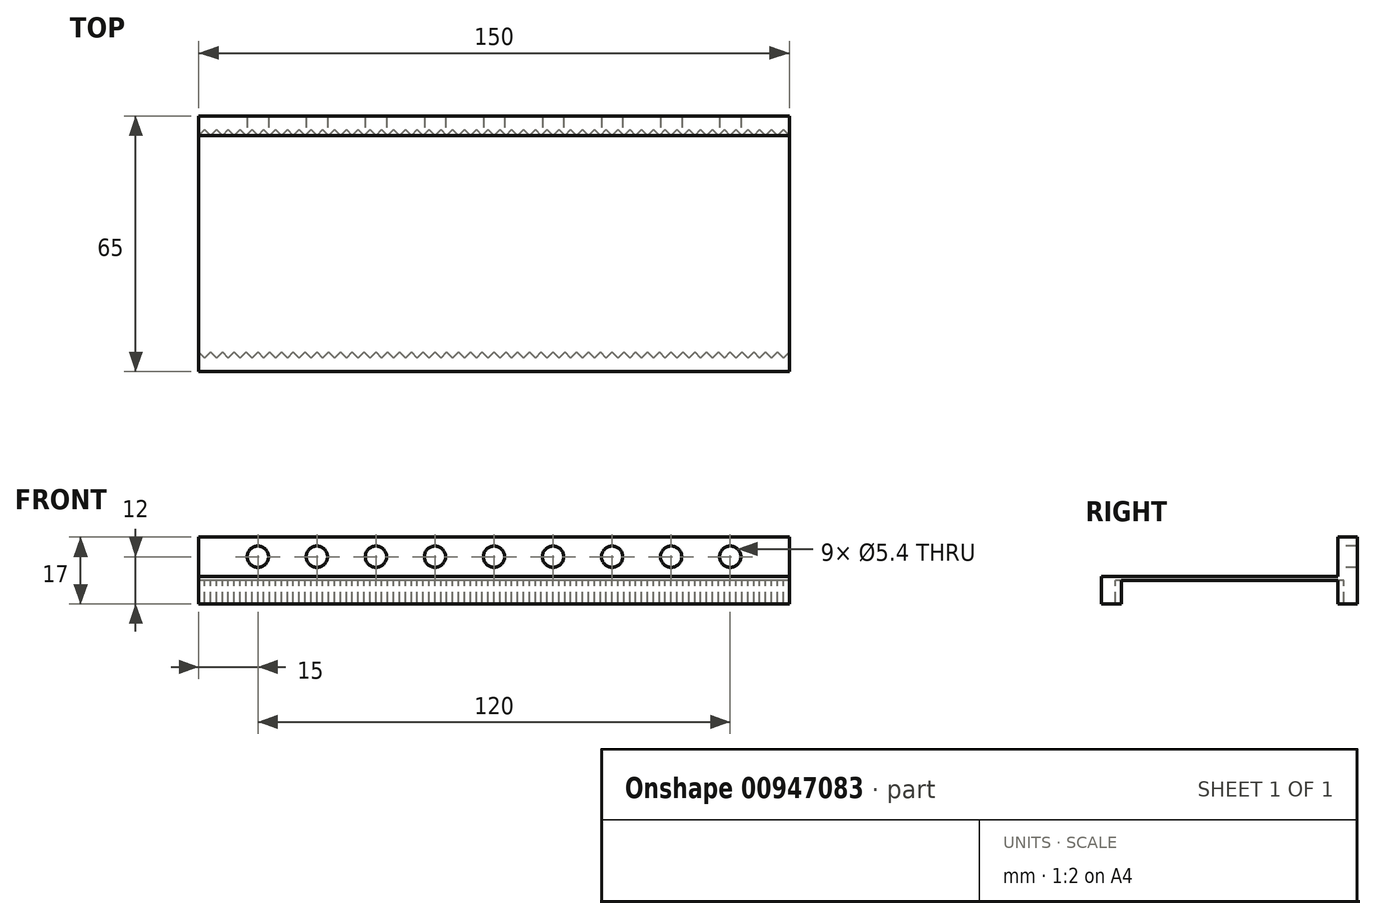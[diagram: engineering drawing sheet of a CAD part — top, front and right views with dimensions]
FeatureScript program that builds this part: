
annotation { "Feature Type Name" : "Feature", "Feature Type Description" : "" }
export const myFeature = defineFeature(function(context is Context, id is Id, definition is map)
    precondition{}
    {
        {
            var Q0;
            Q0=qCreatedBy(makeId("Top.planeOp"),FACE);
            var sketch = newSketch(context, id + "F0", { "sketchPlane" : qUnion([Q0])});
            skLineSegment(sketch, "E0.bottom", {"start": v(75, 32.5) * mm, "end": v(-75, 32.5) * mm});
            skLineSegment(sketch, "E0.top", {"start": v(75, -32.5) * mm, "end": v(-75, -32.5) * mm});
            skLineSegment(sketch, "E0.left", {"start": v(75, 32.5) * mm, "end": v(75, -32.5) * mm});
            skLineSegment(sketch, "E0.right", {"start": v(-75, 32.5) * mm, "end": v(-75, -32.5) * mm});
            skPoint(sketch, "E0.middle", {"position": v(0, 0) * mm});
            skSolve(sketch);
        }
        {
            var Q0;
            Q0 = qSketchRegion(id + "F0", true);
            extrude(context, id + "F1", {"entities" : qUnion([Q0]), "depth" : 1 * mm, "offsetDistance" : 25 * mm});
        }
        {
            var Q0;
            Q0=makeQuery(id+"F1.opExtrude","CAP_FACE",FACE,{"disambiguationData":[OSD([sQuery(id+"F0.wireOp",EDGE,"E0.bottom"),sQuery(id+"F0.wireOp",EDGE,"E0.top"),sQuery(id+"F0.wireOp",EDGE,"E0.left"),sQuery(id+"F0.wireOp",EDGE,"E0.right")])],"isStart":true});
            var sketch = newSketch(context, id + "F2", { "sketchPlane" : qUnion([Q0])});
            skLineSegment(sketch, "E1.bottom", {"start": v(75, -32.5) * mm, "end": v(-75, -32.5) * mm});
            skLineSegment(sketch, "E1.top", {"start": v(75, -27.5) * mm, "end": v(-75, -27.5) * mm, "construction": true});
            skLineSegment(sketch, "E1.left", {"start": v(75, -32.5) * mm, "end": v(75, -27.5) * mm});
            skLineSegment(sketch, "E1.right", {"start": v(-75, -32.5) * mm, "end": v(-75, -27.5) * mm});
            skLineSegment(sketch, "E2.bottom", {"start": v(75, 32.5) * mm, "end": v(-75, 32.5) * mm});
            skLineSegment(sketch, "E2.top", {"start": v(75, 27.5) * mm, "end": v(-75, 27.5) * mm, "construction": true});
            skLineSegment(sketch, "E2.left", {"start": v(75, 32.5) * mm, "end": v(75, 27.5) * mm});
            skLineSegment(sketch, "E2.right", {"start": v(-75, 32.5) * mm, "end": v(-75, 27.5) * mm});
            skLineSegment(sketch, "E3", {"start": v(75, -27.5) * mm, "end": v(73.5, -29) * mm});
            skLineSegment(sketch, "E4", {"start": v(73.5, -29) * mm, "end": v(72, -27.5) * mm});
            skLineSegment(sketch, "E5.1.0.0", {"start": v(72, -27.5) * mm, "end": v(70.5, -29) * mm});
            skLineSegment(sketch, "E5.1.0.1", {"start": v(70.5, -29) * mm, "end": v(69, -27.5) * mm});
            skLineSegment(sketch, "E5.2.0.0", {"start": v(69, -27.5) * mm, "end": v(67.5, -29) * mm});
            skLineSegment(sketch, "E5.2.0.1", {"start": v(67.5, -29) * mm, "end": v(66, -27.5) * mm});
            skLineSegment(sketch, "E5.direction1", {"start": v(73.5, -29) * mm, "end": v(70.5, -29) * mm, "construction": true});
            skLineSegment(sketch, "E6.0.3.0", {"start": v(66, -27.5) * mm, "end": v(64.5, -29) * mm});
            skLineSegment(sketch, "E6.3.3.0", {"start": v(64.5, -29) * mm, "end": v(63, -27.5) * mm});
            skLineSegment(sketch, "E6.0.4.0", {"start": v(63, -27.5) * mm, "end": v(61.5, -29) * mm});
            skLineSegment(sketch, "E6.3.4.0", {"start": v(61.5, -29) * mm, "end": v(60, -27.5) * mm});
            skLineSegment(sketch, "E6.0.5.0", {"start": v(60, -27.5) * mm, "end": v(58.5, -29) * mm});
            skLineSegment(sketch, "E6.3.5.0", {"start": v(58.5, -29) * mm, "end": v(57, -27.5) * mm});
            skLineSegment(sketch, "E6.0.6.0", {"start": v(57, -27.5) * mm, "end": v(55.5, -29) * mm});
            skLineSegment(sketch, "E6.3.6.0", {"start": v(55.5, -29) * mm, "end": v(54, -27.5) * mm});
            skLineSegment(sketch, "E6.0.7.0", {"start": v(54, -27.5) * mm, "end": v(52.5, -29) * mm});
            skLineSegment(sketch, "E6.3.7.0", {"start": v(52.5, -29) * mm, "end": v(51, -27.5) * mm});
            skLineSegment(sketch, "E6.0.8.0", {"start": v(51, -27.5) * mm, "end": v(49.5, -29) * mm});
            skLineSegment(sketch, "E6.3.8.0", {"start": v(49.5, -29) * mm, "end": v(48, -27.5) * mm});
            skLineSegment(sketch, "E6.0.9.0", {"start": v(48, -27.5) * mm, "end": v(46.5, -29) * mm});
            skLineSegment(sketch, "E6.3.9.0", {"start": v(46.5, -29) * mm, "end": v(45, -27.5) * mm});
            skLineSegment(sketch, "E6.0.10.0", {"start": v(45, -27.5) * mm, "end": v(43.5, -29) * mm});
            skLineSegment(sketch, "E6.3.10.0", {"start": v(43.5, -29) * mm, "end": v(42, -27.5) * mm});
            skLineSegment(sketch, "E6.0.11.0", {"start": v(42, -27.5) * mm, "end": v(40.5, -29) * mm});
            skLineSegment(sketch, "E6.3.11.0", {"start": v(40.5, -29) * mm, "end": v(39, -27.5) * mm});
            skLineSegment(sketch, "E6.0.12.0", {"start": v(39, -27.5) * mm, "end": v(37.5, -29) * mm});
            skLineSegment(sketch, "E6.3.12.0", {"start": v(37.5, -29) * mm, "end": v(36, -27.5) * mm});
            skLineSegment(sketch, "E6.0.13.0", {"start": v(36, -27.5) * mm, "end": v(34.5, -29) * mm});
            skLineSegment(sketch, "E6.3.13.0", {"start": v(34.5, -29) * mm, "end": v(33, -27.5) * mm});
            skLineSegment(sketch, "E6.0.14.0", {"start": v(33, -27.5) * mm, "end": v(31.5, -29) * mm});
            skLineSegment(sketch, "E6.3.14.0", {"start": v(31.5, -29) * mm, "end": v(30, -27.5) * mm});
            skLineSegment(sketch, "E6.0.15.0", {"start": v(30, -27.5) * mm, "end": v(28.5, -29) * mm});
            skLineSegment(sketch, "E6.3.15.0", {"start": v(28.5, -29) * mm, "end": v(27, -27.5) * mm});
            skLineSegment(sketch, "E6.0.16.0", {"start": v(27, -27.5) * mm, "end": v(25.5, -29) * mm});
            skLineSegment(sketch, "E6.3.16.0", {"start": v(25.5, -29) * mm, "end": v(24, -27.5) * mm});
            skLineSegment(sketch, "E6.0.17.0", {"start": v(24, -27.5) * mm, "end": v(22.5, -29) * mm});
            skLineSegment(sketch, "E6.3.17.0", {"start": v(22.5, -29) * mm, "end": v(21, -27.5) * mm});
            skLineSegment(sketch, "E6.0.18.0", {"start": v(21, -27.5) * mm, "end": v(19.5, -29) * mm});
            skLineSegment(sketch, "E6.3.18.0", {"start": v(19.5, -29) * mm, "end": v(18, -27.5) * mm});
            skLineSegment(sketch, "E6.0.19.0", {"start": v(18, -27.5) * mm, "end": v(16.5, -29) * mm});
            skLineSegment(sketch, "E6.3.19.0", {"start": v(16.5, -29) * mm, "end": v(15, -27.5) * mm});
            skLineSegment(sketch, "E6.0.20.0", {"start": v(15, -27.5) * mm, "end": v(13.5, -29) * mm});
            skLineSegment(sketch, "E6.3.20.0", {"start": v(13.5, -29) * mm, "end": v(12, -27.5) * mm});
            skLineSegment(sketch, "E6.0.21.0", {"start": v(12, -27.5) * mm, "end": v(10.5, -29) * mm});
            skLineSegment(sketch, "E6.3.21.0", {"start": v(10.5, -29) * mm, "end": v(9, -27.5) * mm});
            skLineSegment(sketch, "E6.0.22.0", {"start": v(9, -27.5) * mm, "end": v(7.5, -29) * mm});
            skLineSegment(sketch, "E6.3.22.0", {"start": v(7.5, -29) * mm, "end": v(6, -27.5) * mm});
            skLineSegment(sketch, "E6.0.23.0", {"start": v(6, -27.5) * mm, "end": v(4.5, -29) * mm});
            skLineSegment(sketch, "E6.3.23.0", {"start": v(4.5, -29) * mm, "end": v(3, -27.5) * mm});
            skLineSegment(sketch, "E6.0.24.0", {"start": v(3, -27.5) * mm, "end": v(1.5, -29) * mm});
            skLineSegment(sketch, "E6.3.24.0", {"start": v(1.5, -29) * mm, "end": v(0, -27.5) * mm});
            skLineSegment(sketch, "E6.0.25.0", {"start": v(0, -27.5) * mm, "end": v(-1.5, -29) * mm});
            skLineSegment(sketch, "E6.3.25.0", {"start": v(-1.5, -29) * mm, "end": v(-3, -27.5) * mm});
            skLineSegment(sketch, "E6.0.26.0", {"start": v(-3, -27.5) * mm, "end": v(-4.5, -29) * mm});
            skLineSegment(sketch, "E6.3.26.0", {"start": v(-4.5, -29) * mm, "end": v(-6, -27.5) * mm});
            skLineSegment(sketch, "E6.0.27.0", {"start": v(-6, -27.5) * mm, "end": v(-7.5, -29) * mm});
            skLineSegment(sketch, "E6.3.27.0", {"start": v(-7.5, -29) * mm, "end": v(-9, -27.5) * mm});
            skLineSegment(sketch, "E6.0.28.0", {"start": v(-9, -27.5) * mm, "end": v(-10.5, -29) * mm});
            skLineSegment(sketch, "E6.3.28.0", {"start": v(-10.5, -29) * mm, "end": v(-12, -27.5) * mm});
            skLineSegment(sketch, "E6.0.29.0", {"start": v(-12, -27.5) * mm, "end": v(-13.5, -29) * mm});
            skLineSegment(sketch, "E6.3.29.0", {"start": v(-13.5, -29) * mm, "end": v(-15, -27.5) * mm});
            skLineSegment(sketch, "E6.0.30.0", {"start": v(-15, -27.5) * mm, "end": v(-16.5, -29) * mm});
            skLineSegment(sketch, "E6.3.30.0", {"start": v(-16.5, -29) * mm, "end": v(-18, -27.5) * mm});
            skLineSegment(sketch, "E6.0.31.0", {"start": v(-18, -27.5) * mm, "end": v(-19.5, -29) * mm});
            skLineSegment(sketch, "E6.3.31.0", {"start": v(-19.5, -29) * mm, "end": v(-21, -27.5) * mm});
            skLineSegment(sketch, "E6.0.32.0", {"start": v(-21, -27.5) * mm, "end": v(-22.5, -29) * mm});
            skLineSegment(sketch, "E6.3.32.0", {"start": v(-22.5, -29) * mm, "end": v(-24, -27.5) * mm});
            skLineSegment(sketch, "E6.0.33.0", {"start": v(-24, -27.5) * mm, "end": v(-25.5, -29) * mm});
            skLineSegment(sketch, "E6.3.33.0", {"start": v(-25.5, -29) * mm, "end": v(-27, -27.5) * mm});
            skLineSegment(sketch, "E6.0.34.0", {"start": v(-27, -27.5) * mm, "end": v(-28.5, -29) * mm});
            skLineSegment(sketch, "E6.3.34.0", {"start": v(-28.5, -29) * mm, "end": v(-30, -27.5) * mm});
            skLineSegment(sketch, "E6.0.35.0", {"start": v(-30, -27.5) * mm, "end": v(-31.5, -29) * mm});
            skLineSegment(sketch, "E6.3.35.0", {"start": v(-31.5, -29) * mm, "end": v(-33, -27.5) * mm});
            skLineSegment(sketch, "E6.0.36.0", {"start": v(-33, -27.5) * mm, "end": v(-34.5, -29) * mm});
            skLineSegment(sketch, "E6.3.36.0", {"start": v(-34.5, -29) * mm, "end": v(-36, -27.5) * mm});
            skLineSegment(sketch, "E6.0.37.0", {"start": v(-36, -27.5) * mm, "end": v(-37.5, -29) * mm});
            skLineSegment(sketch, "E6.3.37.0", {"start": v(-37.5, -29) * mm, "end": v(-39, -27.5) * mm});
            skLineSegment(sketch, "E6.0.38.0", {"start": v(-39, -27.5) * mm, "end": v(-40.5, -29) * mm});
            skLineSegment(sketch, "E6.3.38.0", {"start": v(-40.5, -29) * mm, "end": v(-42, -27.5) * mm});
            skLineSegment(sketch, "E6.0.39.0", {"start": v(-42, -27.5) * mm, "end": v(-43.5, -29) * mm});
            skLineSegment(sketch, "E6.3.39.0", {"start": v(-43.5, -29) * mm, "end": v(-45, -27.5) * mm});
            skLineSegment(sketch, "E6.0.40.0", {"start": v(-45, -27.5) * mm, "end": v(-46.5, -29) * mm});
            skLineSegment(sketch, "E6.3.40.0", {"start": v(-46.5, -29) * mm, "end": v(-48, -27.5) * mm});
            skLineSegment(sketch, "E6.0.41.0", {"start": v(-48, -27.5) * mm, "end": v(-49.5, -29) * mm});
            skLineSegment(sketch, "E6.3.41.0", {"start": v(-49.5, -29) * mm, "end": v(-51, -27.5) * mm});
            skLineSegment(sketch, "E6.0.42.0", {"start": v(-51, -27.5) * mm, "end": v(-52.5, -29) * mm});
            skLineSegment(sketch, "E6.3.42.0", {"start": v(-52.5, -29) * mm, "end": v(-54, -27.5) * mm});
            skLineSegment(sketch, "E6.0.43.0", {"start": v(-54, -27.5) * mm, "end": v(-55.5, -29) * mm});
            skLineSegment(sketch, "E6.3.43.0", {"start": v(-55.5, -29) * mm, "end": v(-57, -27.5) * mm});
            skLineSegment(sketch, "E6.0.44.0", {"start": v(-57, -27.5) * mm, "end": v(-58.5, -29) * mm});
            skLineSegment(sketch, "E6.3.44.0", {"start": v(-58.5, -29) * mm, "end": v(-60, -27.5) * mm});
            skLineSegment(sketch, "E6.0.45.0", {"start": v(-60, -27.5) * mm, "end": v(-61.5, -29) * mm});
            skLineSegment(sketch, "E6.3.45.0", {"start": v(-61.5, -29) * mm, "end": v(-63, -27.5) * mm});
            skLineSegment(sketch, "E6.0.46.0", {"start": v(-63, -27.5) * mm, "end": v(-64.5, -29) * mm});
            skLineSegment(sketch, "E6.3.46.0", {"start": v(-64.5, -29) * mm, "end": v(-66, -27.5) * mm});
            skLineSegment(sketch, "E6.0.47.0", {"start": v(-66, -27.5) * mm, "end": v(-67.5, -29) * mm});
            skLineSegment(sketch, "E6.3.47.0", {"start": v(-67.5, -29) * mm, "end": v(-69, -27.5) * mm});
            skLineSegment(sketch, "E6.0.48.0", {"start": v(-69, -27.5) * mm, "end": v(-70.5, -29) * mm});
            skLineSegment(sketch, "E6.3.48.0", {"start": v(-70.5, -29) * mm, "end": v(-72, -27.5) * mm});
            skLineSegment(sketch, "E6.0.49.0", {"start": v(-72, -27.5) * mm, "end": v(-73.5, -29) * mm});
            skLineSegment(sketch, "E6.3.49.0", {"start": v(-73.5, -29) * mm, "end": v(-75, -27.5) * mm});
            skLineSegment(sketch, "E7", {"start": v(75, 27.5) * mm, "end": v(73.5, 29) * mm});
            skLineSegment(sketch, "E8", {"start": v(73.5, 29) * mm, "end": v(72, 27.5) * mm});
            skLineSegment(sketch, "E9.1.0.0", {"start": v(72, 27.5) * mm, "end": v(70.5, 29) * mm});
            skLineSegment(sketch, "E9.1.0.1", {"start": v(70.5, 29) * mm, "end": v(69, 27.5) * mm});
            skLineSegment(sketch, "E9.2.0.0", {"start": v(69, 27.5) * mm, "end": v(67.5, 29) * mm});
            skLineSegment(sketch, "E9.2.0.1", {"start": v(67.5, 29) * mm, "end": v(66, 27.5) * mm});
            skLineSegment(sketch, "E9.direction1", {"start": v(72, 27.5) * mm, "end": v(69, 27.5) * mm, "construction": true});
            skLineSegment(sketch, "E10.0.3.0", {"start": v(66, 27.5) * mm, "end": v(64.5, 29) * mm});
            skLineSegment(sketch, "E10.3.3.0", {"start": v(64.5, 29) * mm, "end": v(63, 27.5) * mm});
            skLineSegment(sketch, "E10.0.4.0", {"start": v(63, 27.5) * mm, "end": v(61.5, 29) * mm});
            skLineSegment(sketch, "E10.3.4.0", {"start": v(61.5, 29) * mm, "end": v(60, 27.5) * mm});
            skLineSegment(sketch, "E10.0.5.0", {"start": v(60, 27.5) * mm, "end": v(58.5, 29) * mm});
            skLineSegment(sketch, "E10.3.5.0", {"start": v(58.5, 29) * mm, "end": v(57, 27.5) * mm});
            skLineSegment(sketch, "E10.0.6.0", {"start": v(57, 27.5) * mm, "end": v(55.5, 29) * mm});
            skLineSegment(sketch, "E10.3.6.0", {"start": v(55.5, 29) * mm, "end": v(54, 27.5) * mm});
            skLineSegment(sketch, "E10.0.7.0", {"start": v(54, 27.5) * mm, "end": v(52.5, 29) * mm});
            skLineSegment(sketch, "E10.3.7.0", {"start": v(52.5, 29) * mm, "end": v(51, 27.5) * mm});
            skLineSegment(sketch, "E10.0.8.0", {"start": v(51, 27.5) * mm, "end": v(49.5, 29) * mm});
            skLineSegment(sketch, "E10.3.8.0", {"start": v(49.5, 29) * mm, "end": v(48, 27.5) * mm});
            skLineSegment(sketch, "E10.0.9.0", {"start": v(48, 27.5) * mm, "end": v(46.5, 29) * mm});
            skLineSegment(sketch, "E10.3.9.0", {"start": v(46.5, 29) * mm, "end": v(45, 27.5) * mm});
            skLineSegment(sketch, "E10.0.10.0", {"start": v(45, 27.5) * mm, "end": v(43.5, 29) * mm});
            skLineSegment(sketch, "E10.3.10.0", {"start": v(43.5, 29) * mm, "end": v(42, 27.5) * mm});
            skLineSegment(sketch, "E10.0.11.0", {"start": v(42, 27.5) * mm, "end": v(40.5, 29) * mm});
            skLineSegment(sketch, "E10.3.11.0", {"start": v(40.5, 29) * mm, "end": v(39, 27.5) * mm});
            skLineSegment(sketch, "E10.0.12.0", {"start": v(39, 27.5) * mm, "end": v(37.5, 29) * mm});
            skLineSegment(sketch, "E10.3.12.0", {"start": v(37.5, 29) * mm, "end": v(36, 27.5) * mm});
            skLineSegment(sketch, "E10.0.13.0", {"start": v(36, 27.5) * mm, "end": v(34.5, 29) * mm});
            skLineSegment(sketch, "E10.3.13.0", {"start": v(34.5, 29) * mm, "end": v(33, 27.5) * mm});
            skLineSegment(sketch, "E10.0.14.0", {"start": v(33, 27.5) * mm, "end": v(31.5, 29) * mm});
            skLineSegment(sketch, "E10.3.14.0", {"start": v(31.5, 29) * mm, "end": v(30, 27.5) * mm});
            skLineSegment(sketch, "E10.0.15.0", {"start": v(30, 27.5) * mm, "end": v(28.5, 29) * mm});
            skLineSegment(sketch, "E10.3.15.0", {"start": v(28.5, 29) * mm, "end": v(27, 27.5) * mm});
            skLineSegment(sketch, "E10.0.16.0", {"start": v(27, 27.5) * mm, "end": v(25.5, 29) * mm});
            skLineSegment(sketch, "E10.3.16.0", {"start": v(25.5, 29) * mm, "end": v(24, 27.5) * mm});
            skLineSegment(sketch, "E10.0.17.0", {"start": v(24, 27.5) * mm, "end": v(22.5, 29) * mm});
            skLineSegment(sketch, "E10.3.17.0", {"start": v(22.5, 29) * mm, "end": v(21, 27.5) * mm});
            skLineSegment(sketch, "E10.0.18.0", {"start": v(21, 27.5) * mm, "end": v(19.5, 29) * mm});
            skLineSegment(sketch, "E10.3.18.0", {"start": v(19.5, 29) * mm, "end": v(18, 27.5) * mm});
            skLineSegment(sketch, "E10.0.19.0", {"start": v(18, 27.5) * mm, "end": v(16.5, 29) * mm});
            skLineSegment(sketch, "E10.3.19.0", {"start": v(16.5, 29) * mm, "end": v(15, 27.5) * mm});
            skLineSegment(sketch, "E10.0.20.0", {"start": v(15, 27.5) * mm, "end": v(13.5, 29) * mm});
            skLineSegment(sketch, "E10.3.20.0", {"start": v(13.5, 29) * mm, "end": v(12, 27.5) * mm});
            skLineSegment(sketch, "E10.0.21.0", {"start": v(12, 27.5) * mm, "end": v(10.5, 29) * mm});
            skLineSegment(sketch, "E10.3.21.0", {"start": v(10.5, 29) * mm, "end": v(9, 27.5) * mm});
            skLineSegment(sketch, "E10.0.22.0", {"start": v(9, 27.5) * mm, "end": v(7.5, 29) * mm});
            skLineSegment(sketch, "E10.3.22.0", {"start": v(7.5, 29) * mm, "end": v(6, 27.5) * mm});
            skLineSegment(sketch, "E10.0.23.0", {"start": v(6, 27.5) * mm, "end": v(4.5, 29) * mm});
            skLineSegment(sketch, "E10.3.23.0", {"start": v(4.5, 29) * mm, "end": v(3, 27.5) * mm});
            skLineSegment(sketch, "E10.0.24.0", {"start": v(3, 27.5) * mm, "end": v(1.5, 29) * mm});
            skLineSegment(sketch, "E10.3.24.0", {"start": v(1.5, 29) * mm, "end": v(0, 27.5) * mm});
            skLineSegment(sketch, "E10.0.25.0", {"start": v(0, 27.5) * mm, "end": v(-1.5, 29) * mm});
            skLineSegment(sketch, "E10.3.25.0", {"start": v(-1.5, 29) * mm, "end": v(-3, 27.5) * mm});
            skLineSegment(sketch, "E10.0.26.0", {"start": v(-3, 27.5) * mm, "end": v(-4.5, 29) * mm});
            skLineSegment(sketch, "E10.3.26.0", {"start": v(-4.5, 29) * mm, "end": v(-6, 27.5) * mm});
            skLineSegment(sketch, "E10.0.27.0", {"start": v(-6, 27.5) * mm, "end": v(-7.5, 29) * mm});
            skLineSegment(sketch, "E10.3.27.0", {"start": v(-7.5, 29) * mm, "end": v(-9, 27.5) * mm});
            skLineSegment(sketch, "E10.0.28.0", {"start": v(-9, 27.5) * mm, "end": v(-10.5, 29) * mm});
            skLineSegment(sketch, "E10.3.28.0", {"start": v(-10.5, 29) * mm, "end": v(-12, 27.5) * mm});
            skLineSegment(sketch, "E10.0.29.0", {"start": v(-12, 27.5) * mm, "end": v(-13.5, 29) * mm});
            skLineSegment(sketch, "E10.3.29.0", {"start": v(-13.5, 29) * mm, "end": v(-15, 27.5) * mm});
            skLineSegment(sketch, "E10.0.30.0", {"start": v(-15, 27.5) * mm, "end": v(-16.5, 29) * mm});
            skLineSegment(sketch, "E10.3.30.0", {"start": v(-16.5, 29) * mm, "end": v(-18, 27.5) * mm});
            skLineSegment(sketch, "E10.0.31.0", {"start": v(-18, 27.5) * mm, "end": v(-19.5, 29) * mm});
            skLineSegment(sketch, "E10.3.31.0", {"start": v(-19.5, 29) * mm, "end": v(-21, 27.5) * mm});
            skLineSegment(sketch, "E10.0.32.0", {"start": v(-21, 27.5) * mm, "end": v(-22.5, 29) * mm});
            skLineSegment(sketch, "E10.3.32.0", {"start": v(-22.5, 29) * mm, "end": v(-24, 27.5) * mm});
            skLineSegment(sketch, "E10.0.33.0", {"start": v(-24, 27.5) * mm, "end": v(-25.5, 29) * mm});
            skLineSegment(sketch, "E10.3.33.0", {"start": v(-25.5, 29) * mm, "end": v(-27, 27.5) * mm});
            skLineSegment(sketch, "E10.0.34.0", {"start": v(-27, 27.5) * mm, "end": v(-28.5, 29) * mm});
            skLineSegment(sketch, "E10.3.34.0", {"start": v(-28.5, 29) * mm, "end": v(-30, 27.5) * mm});
            skLineSegment(sketch, "E10.0.35.0", {"start": v(-30, 27.5) * mm, "end": v(-31.5, 29) * mm});
            skLineSegment(sketch, "E10.3.35.0", {"start": v(-31.5, 29) * mm, "end": v(-33, 27.5) * mm});
            skLineSegment(sketch, "E10.0.36.0", {"start": v(-33, 27.5) * mm, "end": v(-34.5, 29) * mm});
            skLineSegment(sketch, "E10.3.36.0", {"start": v(-34.5, 29) * mm, "end": v(-36, 27.5) * mm});
            skLineSegment(sketch, "E10.0.37.0", {"start": v(-36, 27.5) * mm, "end": v(-37.5, 29) * mm});
            skLineSegment(sketch, "E10.3.37.0", {"start": v(-37.5, 29) * mm, "end": v(-39, 27.5) * mm});
            skLineSegment(sketch, "E10.0.38.0", {"start": v(-39, 27.5) * mm, "end": v(-40.5, 29) * mm});
            skLineSegment(sketch, "E10.3.38.0", {"start": v(-40.5, 29) * mm, "end": v(-42, 27.5) * mm});
            skLineSegment(sketch, "E10.0.39.0", {"start": v(-42, 27.5) * mm, "end": v(-43.5, 29) * mm});
            skLineSegment(sketch, "E10.3.39.0", {"start": v(-43.5, 29) * mm, "end": v(-45, 27.5) * mm});
            skLineSegment(sketch, "E10.0.40.0", {"start": v(-45, 27.5) * mm, "end": v(-46.5, 29) * mm});
            skLineSegment(sketch, "E10.3.40.0", {"start": v(-46.5, 29) * mm, "end": v(-48, 27.5) * mm});
            skLineSegment(sketch, "E10.0.41.0", {"start": v(-48, 27.5) * mm, "end": v(-49.5, 29) * mm});
            skLineSegment(sketch, "E10.3.41.0", {"start": v(-49.5, 29) * mm, "end": v(-51, 27.5) * mm});
            skLineSegment(sketch, "E10.0.42.0", {"start": v(-51, 27.5) * mm, "end": v(-52.5, 29) * mm});
            skLineSegment(sketch, "E10.3.42.0", {"start": v(-52.5, 29) * mm, "end": v(-54, 27.5) * mm});
            skLineSegment(sketch, "E10.0.43.0", {"start": v(-54, 27.5) * mm, "end": v(-55.5, 29) * mm});
            skLineSegment(sketch, "E10.3.43.0", {"start": v(-55.5, 29) * mm, "end": v(-57, 27.5) * mm});
            skLineSegment(sketch, "E10.0.44.0", {"start": v(-57, 27.5) * mm, "end": v(-58.5, 29) * mm});
            skLineSegment(sketch, "E10.3.44.0", {"start": v(-58.5, 29) * mm, "end": v(-60, 27.5) * mm});
            skLineSegment(sketch, "E10.0.45.0", {"start": v(-60, 27.5) * mm, "end": v(-61.5, 29) * mm});
            skLineSegment(sketch, "E10.3.45.0", {"start": v(-61.5, 29) * mm, "end": v(-63, 27.5) * mm});
            skLineSegment(sketch, "E10.0.46.0", {"start": v(-63, 27.5) * mm, "end": v(-64.5, 29) * mm});
            skLineSegment(sketch, "E10.3.46.0", {"start": v(-64.5, 29) * mm, "end": v(-66, 27.5) * mm});
            skLineSegment(sketch, "E10.0.47.0", {"start": v(-66, 27.5) * mm, "end": v(-67.5, 29) * mm});
            skLineSegment(sketch, "E10.3.47.0", {"start": v(-67.5, 29) * mm, "end": v(-69, 27.5) * mm});
            skLineSegment(sketch, "E10.0.48.0", {"start": v(-69, 27.5) * mm, "end": v(-70.5, 29) * mm});
            skLineSegment(sketch, "E10.3.48.0", {"start": v(-70.5, 29) * mm, "end": v(-72, 27.5) * mm});
            skLineSegment(sketch, "E10.0.49.0", {"start": v(-72, 27.5) * mm, "end": v(-73.5, 29) * mm});
            skLineSegment(sketch, "E10.3.49.0", {"start": v(-73.5, 29) * mm, "end": v(-75, 27.5) * mm});
            skSolve(sketch);
        }
        {
            var Q0;
            Q0 = qSketchRegion(id + "F2", true);
            extrude(context, id + "F3", {"entities" : qUnion([Q0]), "operationType" : NewBodyOperationType.ADD, "depth" : 6 * mm, "offsetDistance" : 25 * mm});
        }
        {
            var Q0;
            Q0=makeQuery(id+"F1.opExtrude","CAP_FACE",FACE,{"disambiguationData":[OSD([sQuery(id+"F0.wireOp",EDGE,"E0.bottom"),sQuery(id+"F0.wireOp",EDGE,"E0.top"),sQuery(id+"F0.wireOp",EDGE,"E0.left"),sQuery(id+"F0.wireOp",EDGE,"E0.right")])],"isStart":false});
            var sketch = newSketch(context, id + "F4", { "sketchPlane" : qUnion([Q0])});
            skLineSegment(sketch, "E11.bottom", {"start": v(-75, 32.5) * mm, "end": v(75, 32.5) * mm});
            skLineSegment(sketch, "E11.top", {"start": v(-75, 27.5) * mm, "end": v(75, 27.5) * mm});
            skLineSegment(sketch, "E11.left", {"start": v(-75, 32.5) * mm, "end": v(-75, 27.5) * mm});
            skLineSegment(sketch, "E11.right", {"start": v(75, 32.5) * mm, "end": v(75, 27.5) * mm});
            skSolve(sketch);
        }
        {
            var Q0;
            Q0 = qSketchRegion(id + "F4", true);
            extrude(context, id + "F5", {"entities" : qUnion([Q0]), "operationType" : NewBodyOperationType.ADD, "depth" : 10 * mm, "offsetDistance" : 25 * mm});
        }
        {
            var Q0;
            Q0=makeQuery(id+"F5.opExtrude","SWEPT_FACE",FACE,{"disambiguationData":[OSD([sQuery(id+"F4.wireOp",EDGE,"E11.top")])]});
            var sketch = newSketch(context, id + "F6", { "sketchPlane" : qUnion([Q0])});
            skLineSegment(sketch, "E12", {"start": v(-75, 6) * mm, "end": v(75, 6) * mm, "construction": true});
            skCircle(sketch, "E13", {"center": v(-60, 6) * mm, "radius": 2.7 * mm});
            skCircle(sketch, "E14.1.0.0", {"center": v(-45, 6) * mm, "radius": 2.7 * mm});
            skCircle(sketch, "E14.2.0.0", {"center": v(-30, 6) * mm, "radius": 2.7 * mm});
            skCircle(sketch, "E14.3.0.0", {"center": v(-15, 6) * mm, "radius": 2.7 * mm});
            skCircle(sketch, "E14.4.0.0", {"center": v(0, 6) * mm, "radius": 2.7 * mm});
            skCircle(sketch, "E14.5.0.0", {"center": v(15, 6) * mm, "radius": 2.7 * mm});
            skCircle(sketch, "E14.6.0.0", {"center": v(30, 6) * mm, "radius": 2.7 * mm});
            skCircle(sketch, "E14.7.0.0", {"center": v(45, 6) * mm, "radius": 2.7 * mm});
            skCircle(sketch, "E14.8.0.0", {"center": v(60, 6) * mm, "radius": 2.7 * mm});
            skLineSegment(sketch, "E14.direction1", {"start": v(-60, 6) * mm, "end": v(-45, 6) * mm, "construction": true});
            skSolve(sketch);
        }
        {
            var Q0;
            Q0 = qSketchRegion(id + "F6", true);
            extrude(context, id + "F7", {"entities" : qUnion([Q0]), "operationType" : NewBodyOperationType.REMOVE, "oppositeDirection" : true, "depth" : 25 * mm, "offsetDistance" : 25 * mm});
        }
    });
